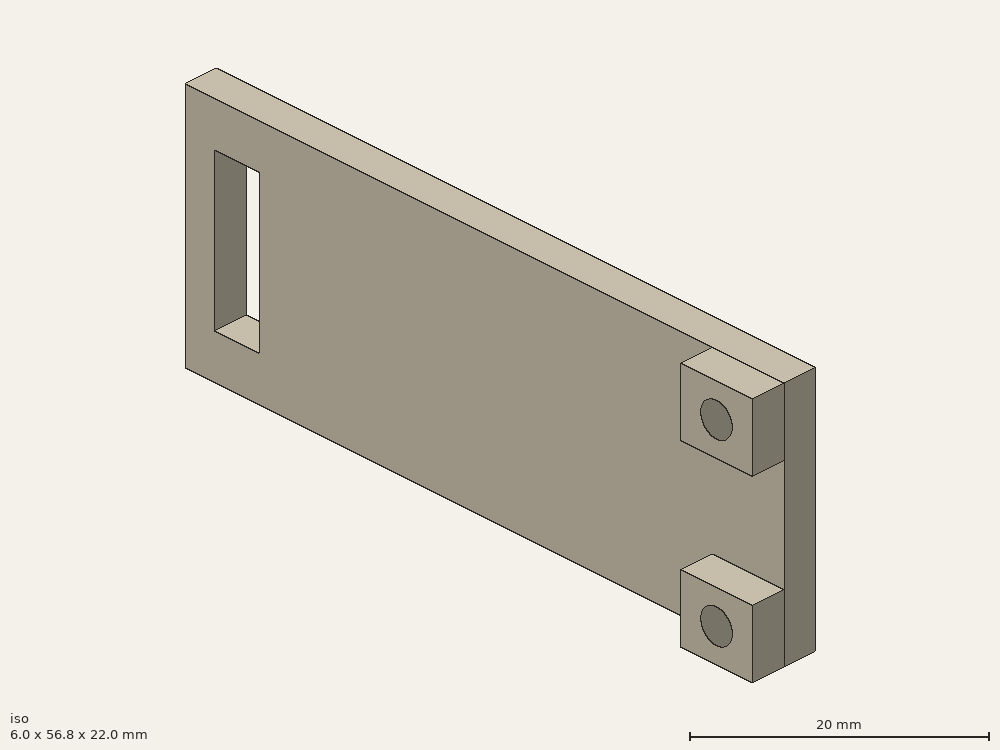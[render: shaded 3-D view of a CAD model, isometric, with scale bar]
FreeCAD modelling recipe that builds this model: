
FCSTD DOCUMENT  (FreeCAD 0.18.4R)
Label: 3d-printer-pdb-din-rail-mount-16mm
License: All rights reserved
LicenseURL: http://en.wikipedia.org/wiki/All_rights_reserved
objects: Part::Feature×5, Part::Box×5, Part::Cut×4, Part::MultiFuse×3, Part::Cylinder×2, Mesh::Feature×1
note: 19 computed .brp shape members not serialized (recipe doc carries the construction recipe); baked Part::Feature solids carry a one-line shape summary decoded from their .brp

FEATURE [Mesh::Feature] PCB_din_clip
FEATURE [Part::Feature] PCB_din_clip001
  shape: bbox 26.19 x 68.23 x 6 mm, 300 faces, 0 solids (baked)
FEATURE [Part::Box] Box  label="Cube"
  AttacherType = Attacher::AttachEngine3D
  Height = 10
  Length = 10
  Placement = pos=(-10,-38,-3) rot=(0,0,1;0rad)
  Width = 84
FEATURE [Part::Cut] Cut
  Base = -> PCB_din_clip001
  Placement = pos=(0,0,-1) rot=(0,0,1;0rad)
  Tool = -> Box
FEATURE [Part::Box] Box002  label="Cube002"
  AttacherType = Attacher::AttachEngine3D
  Height = 14
  Length = 10
  Placement = pos=(-7,22.2,0) rot=(0,0,1;0rad)
  Width = 4.2
FEATURE [Part::Box] Box003  label="Cube003"
  AttacherType = Attacher::AttachEngine3D
  Height = 6
  Length = 3
  Placement = pos=(-6,-27.6,12) rot=(0,0,1;0rad)
  Width = 6.8
FEATURE [Part::Cylinder] Cylinder
  Angle = 360
  AttacherType = Attacher::AttachEngine3D
  Height = 14
  Placement = pos=(-13,-24.2,15) rot=(0,1,0;1.5708rad)
  Radius = 1.5
FEATURE [Part::Box] Box004  label="Cube004"
  AttacherType = Attacher::AttachEngine3D
  Height = 22
  Length = 3
  Placement = pos=(-3,-27.6,-4) rot=(0,0,1;0rad)
  Width = 56.8
FEATURE [Part::Box] Box005  label="Cube005"
  AttacherType = Attacher::AttachEngine3D
  Height = 6
  Length = 3
  Placement = pos=(-6,-27.6,-4) rot=(0,0,1;0rad)
  Width = 6.8
FEATURE [Part::Cylinder] Cylinder001
  Angle = 360
  AttacherType = Attacher::AttachEngine3D
  Height = 14
  Placement = pos=(-13,-24.2,-1) rot=(0,1,0;1.5708rad)
  Radius = 1.5
FEATURE [Part::Feature] Cut_solid  label="Cut (Solid)"
  shape: bbox 19.19 x 42.37 x 6 mm, 130 faces (baked)
FEATURE [Part::Feature] Cut_solid001  label="Cut (Solid)001"
  Placement = pos=(0,0,6) rot=(0,0,1;0rad)
  shape: bbox 19.19 x 42.37 x 6 mm, 130 faces (baked)
FEATURE [Part::Feature] Cut_solid002  label="Cut (Solid)002"
  Placement = pos=(0,0,12) rot=(0,0,1;0rad)
  shape: bbox 19.19 x 42.37 x 6 mm, 130 faces (baked)
FEATURE [Part::Feature] Cut_solid003  label="Cut (Solid)003"
  Placement = pos=(0,0,16) rot=(0,0,1;0rad)
  shape: bbox 19.19 x 42.37 x 6 mm, 130 faces (baked)
FEATURE [Part::MultiFuse] Fusion
  Shapes = -> [Cut_solid003,Cut_solid,Cut_solid001,Cut_solid002]
FEATURE [Part::MultiFuse] Fusion001
  Shapes = -> [Box004,Box005,Box003]
FEATURE [Part::Cut] Cut001
  Base = -> Fusion001
  Tool = -> Cylinder
FEATURE [Part::Cut] Cut002
  Base = -> Cut001
  Tool = -> Cylinder001
FEATURE [Part::Cut] Cut003
  Base = -> Cut002
  Tool = -> Box002
FEATURE [Part::MultiFuse] Fusion002
  Shapes = -> [Fusion,Cut003]
